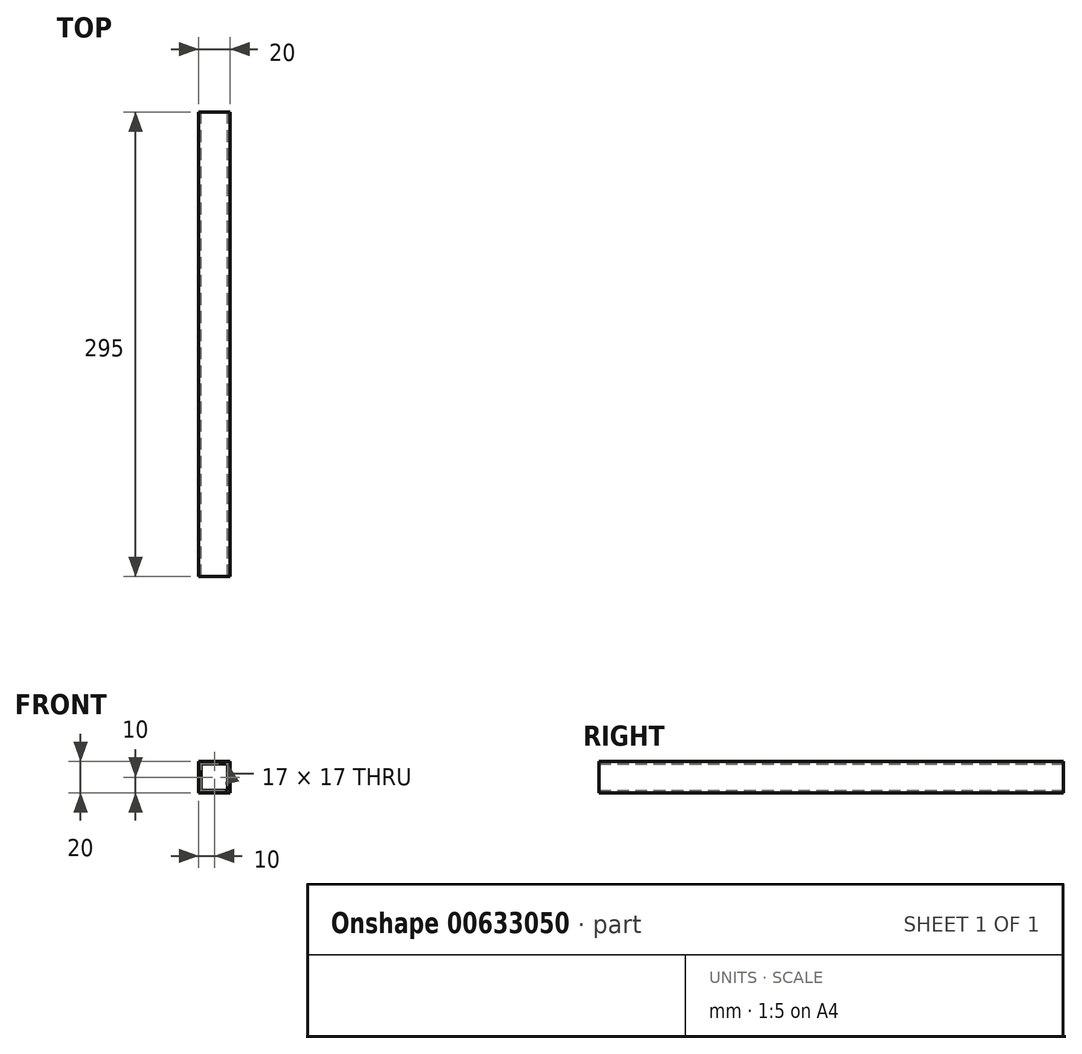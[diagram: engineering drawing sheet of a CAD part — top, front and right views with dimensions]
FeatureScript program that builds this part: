
annotation { "Feature Type Name" : "Feature", "Feature Type Description" : "" }
export const myFeature = defineFeature(function(context is Context, id is Id, definition is map)
    precondition{}
    {
        {
            var Q0;
            Q0=qCreatedBy(makeId("Front.planeOp"),FACE);
            var sketch = newSketch(context, id + "F0", { "sketchPlane" : qUnion([Q0])});
            skLineSegment(sketch, "E0.bottom", {"start": v(0, 0) * mm, "end": v(20, 0) * mm});
            skLineSegment(sketch, "E0.top", {"start": v(0, -20) * mm, "end": v(20, -20) * mm});
            skLineSegment(sketch, "E0.left", {"start": v(0, 0) * mm, "end": v(0, -20) * mm});
            skLineSegment(sketch, "E0.right", {"start": v(20, 0) * mm, "end": v(20, -20) * mm});
            skLineSegment(sketch, "E1.0", {"start": v(1.5, -1.5) * mm, "end": v(18.5, -1.5) * mm});
            skLineSegment(sketch, "E1.1", {"start": v(1.5, -1.5) * mm, "end": v(1.5, -18.5) * mm});
            skLineSegment(sketch, "E1.2", {"start": v(1.5, -18.5) * mm, "end": v(18.5, -18.5) * mm});
            skLineSegment(sketch, "E1.3", {"start": v(18.5, -1.5) * mm, "end": v(18.5, -18.5) * mm});
            skSolve(sketch);
        }
        {
            var Q0;
            Q0=makeQuery(id+"F0.imprint","IMPRINT",FACE,{"disambiguationData":[TD([[makeQuery(id+"F0.imprint","IMPRINT",EDGE,{"derivedFrom":sQuery(id+"F0.wireOp",EDGE,"E0.bottom")}),-1.0]])]});
            extrude(context, id + "F1", {"entities" : qUnion([Q0]), "depth" : 295 * mm, "offsetDistance" : 25 * mm});
        }
    });
